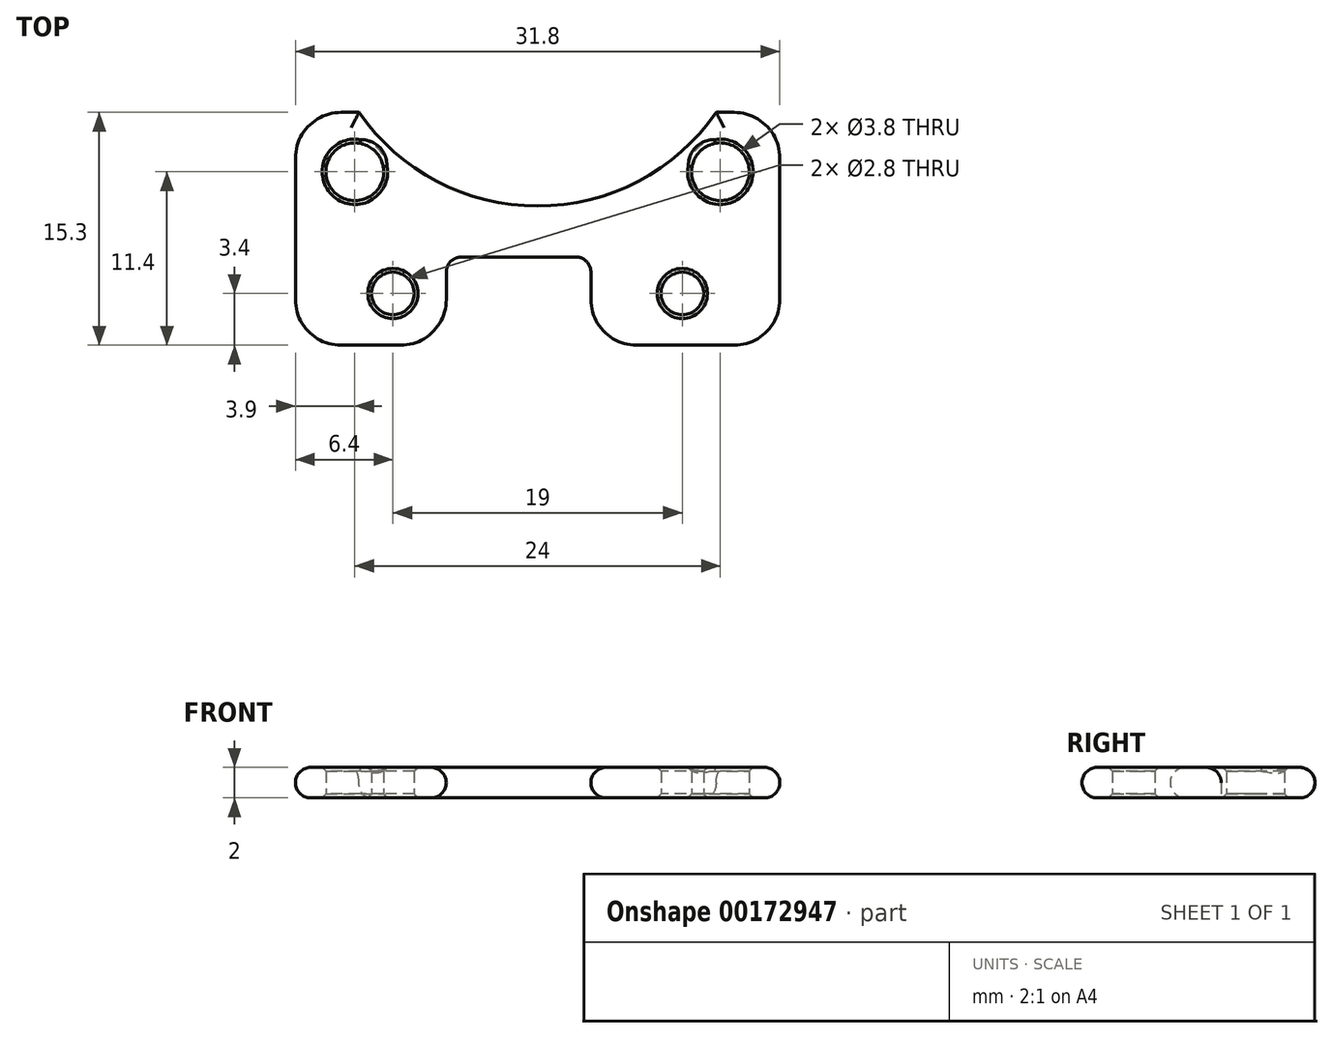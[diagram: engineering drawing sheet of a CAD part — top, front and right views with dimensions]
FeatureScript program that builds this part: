
annotation { "Feature Type Name" : "Feature", "Feature Type Description" : "" }
export const myFeature = defineFeature(function(context is Context, id is Id, definition is map)
    precondition{}
    {
        {
            var Q0;
            Q0=qCreatedBy(makeId("Top.planeOp"),FACE);
            var sketch = newSketch(context, id + "F0", { "sketchPlane" : qUnion([Q0])});
            skPoint(sketch, "E0.middle", {"position": v(0, 0) * mm});
            skCircle(sketch, "E1", {"center": v(-12, 4) * mm, "radius": 1.9 * mm});
            skCircle(sketch, "E2", {"center": v(12, 4) * mm, "radius": 1.9 * mm});
            skCircle(sketch, "E3", {"center": v(-9.5, -4) * mm, "radius": 1.4 * mm});
            skCircle(sketch, "E4", {"center": v(9.5, -4) * mm, "radius": 1.4 * mm});
            skLineSegment(sketch, "E5.bottom", {"start": v(-12.9, 7.9) * mm, "end": v(-11.72, 7.9) * mm});
            skLineSegment(sketch, "E5.top", {"start": v(-12.9, -7.4) * mm, "end": v(-9, -7.4) * mm});
            skLineSegment(sketch, "E5.left", {"start": v(-15.9, 4.9) * mm, "end": v(-15.9, -4.4) * mm});
            skLineSegment(sketch, "E5.right", {"start": v(15.9, 4.9) * mm, "end": v(15.9, -4.4) * mm});
            skPoint(sketch, "E6.visualSharp", {"position": v(-15.9, 7.9) * mm});
            skArc(sketch, "E6.filletArc", {"start": v(-12.9, 7.9) * mm, "mid": v(-15.02, 7.02) * mm, "end": v(-15.9, 4.9) * mm});
            skPoint(sketch, "E7.visualSharp", {"position": v(15.9, 7.9) * mm});
            skArc(sketch, "E7.filletArc", {"start": v(15.9, 4.9) * mm, "mid": v(15.02, 7.02) * mm, "end": v(12.9, 7.9) * mm});
            skPoint(sketch, "E8.visualSharp", {"position": v(15.9, -7.4) * mm});
            skArc(sketch, "E8.filletArc", {"start": v(12.9, -7.4) * mm, "mid": v(15.02, -6.52) * mm, "end": v(15.9, -4.4) * mm});
            skPoint(sketch, "E9.visualSharp", {"position": v(-15.9, -7.4) * mm});
            skArc(sketch, "E9.filletArc", {"start": v(-15.9, -4.4) * mm, "mid": v(-15.02, -6.52) * mm, "end": v(-12.9, -7.4) * mm});
            skPoint(sketch, "E10", {"position": v(-15, 1) * mm});
            skArc(sketch, "E11", {"start": v(-11.72, 7.9) * mm, "mid": v(0, 1.75) * mm, "end": v(11.72, 7.9) * mm});
            skLineSegment(sketch, "E12.trimOffspring", {"start": v(11.72, 7.9) * mm, "end": v(12.9, 7.9) * mm});
            skLineSegment(sketch, "E13", {"start": v(-6, -4.4) * mm, "end": v(-6, -2.6) * mm});
            skLineSegment(sketch, "E14", {"start": v(-5, -1.6) * mm, "end": v(2.5, -1.6) * mm});
            skLineSegment(sketch, "E15", {"start": v(3.5, -2.6) * mm, "end": v(3.5, -4.4) * mm});
            skLineSegment(sketch, "E16.trimOffspring", {"start": v(6.5, -7.4) * mm, "end": v(12.9, -7.4) * mm});
            skPoint(sketch, "E17.visualSharp", {"position": v(-6, -7.4) * mm});
            skArc(sketch, "E17.filletArc", {"start": v(-9, -7.4) * mm, "mid": v(-6.88, -6.52) * mm, "end": v(-6, -4.4) * mm});
            skPoint(sketch, "E18.visualSharp", {"position": v(3.5, -7.4) * mm});
            skArc(sketch, "E18.filletArc", {"start": v(3.5, -4.4) * mm, "mid": v(4.38, -6.52) * mm, "end": v(6.5, -7.4) * mm});
            skPoint(sketch, "E19.visualSharp", {"position": v(-6, -1.6) * mm});
            skArc(sketch, "E19.filletArc", {"start": v(-5, -1.6) * mm, "mid": v(-5.7, -1.9) * mm, "end": v(-6, -2.6) * mm});
            skPoint(sketch, "E20.visualSharp", {"position": v(3.5, -1.6) * mm});
            skArc(sketch, "E20.filletArc", {"start": v(3.5, -2.6) * mm, "mid": v(3.2, -1.9) * mm, "end": v(2.5, -1.6) * mm});
            skSolve(sketch);
        }
        {
            var Q0;
            Q0=makeQuery(id+"F0.imprint","IMPRINT",FACE,{"disambiguationData":[TD([[makeQuery(id+"F0.imprint","IMPRINT",EDGE,{"derivedFrom":sQuery(id+"F0.wireOp",EDGE,"E1")}),-1.0]])]});
            extrude(context, id + "F1", {"entities" : qUnion([Q0]), "depth" : 2 * mm});
        }
        {
            var Q0;
            Q0=makeQuery(id+"F1.opExtrude","CAP_EDGE",EDGE,{"disambiguationData":[OSD([sQuery(id+"F0.wireOp",EDGE,"E7.filletArc")])],"isStart":false});
            var Q1;
            Q1=makeQuery(id+"F1.opExtrude","CAP_EDGE",EDGE,{"disambiguationData":[OSD([sQuery(id+"F0.wireOp",EDGE,"E6.filletArc")])],"isStart":true});
            var Q2;
            Q2=makeQuery(id+"F1.opExtrude","CAP_EDGE",EDGE,{"disambiguationData":[OSD([sQuery(id+"F0.wireOp",EDGE,"E11")])],"isStart":false});
            fillet(context, id + "F2", {"entities" : qUnion([Q0, Q1, Q2]), "radius" : 1 * mm, "tangentPropagation" : true, "allowEdgeOverflow" : false});
        }
        {
            var Q0;
            Q0=makeQuery(id+"F1.opExtrude","CAP_EDGE",EDGE,{"disambiguationData":[OSD([sQuery(id+"F0.wireOp",EDGE,"E2")])],"isStart":true});
            var Q1;
            Q1=makeQuery(id+"F1.opExtrude","CAP_EDGE",EDGE,{"disambiguationData":[OSD([sQuery(id+"F0.wireOp",EDGE,"E1")])],"isStart":true});
            var Q2;
            Q2=makeQuery(id+"F1.opExtrude","CAP_EDGE",EDGE,{"disambiguationData":[OSD([sQuery(id+"F0.wireOp",EDGE,"E3")])],"isStart":false});
            var Q3;
            Q3=makeQuery(id+"F1.opExtrude","CAP_EDGE",EDGE,{"disambiguationData":[OSD([sQuery(id+"F0.wireOp",EDGE,"E4")])],"isStart":true});
            var Q4;
            Q4=makeQuery(id+"F1.opExtrude","CAP_EDGE",EDGE,{"disambiguationData":[OSD([sQuery(id+"F0.wireOp",EDGE,"E2")])],"isStart":false});
            var Q5;
            Q5=makeQuery(id+"F1.opExtrude","CAP_EDGE",EDGE,{"disambiguationData":[OSD([sQuery(id+"F0.wireOp",EDGE,"E4")])],"isStart":false});
            var Q6;
            Q6=makeQuery(id+"F1.opExtrude","CAP_EDGE",EDGE,{"disambiguationData":[OSD([sQuery(id+"F0.wireOp",EDGE,"E3")])],"isStart":true});
            var Q7;
            Q7=makeQuery(id+"F1.opExtrude","CAP_EDGE",EDGE,{"disambiguationData":[OSD([sQuery(id+"F0.wireOp",EDGE,"E1")])],"isStart":false});
            chamfer(context, id + "F3", {"entities" : qUnion([Q0, Q1, Q2, Q3, Q4, Q5, Q6, Q7]), "width" : .25 * mm, "tangentPropagation" : true});
        }
    });
